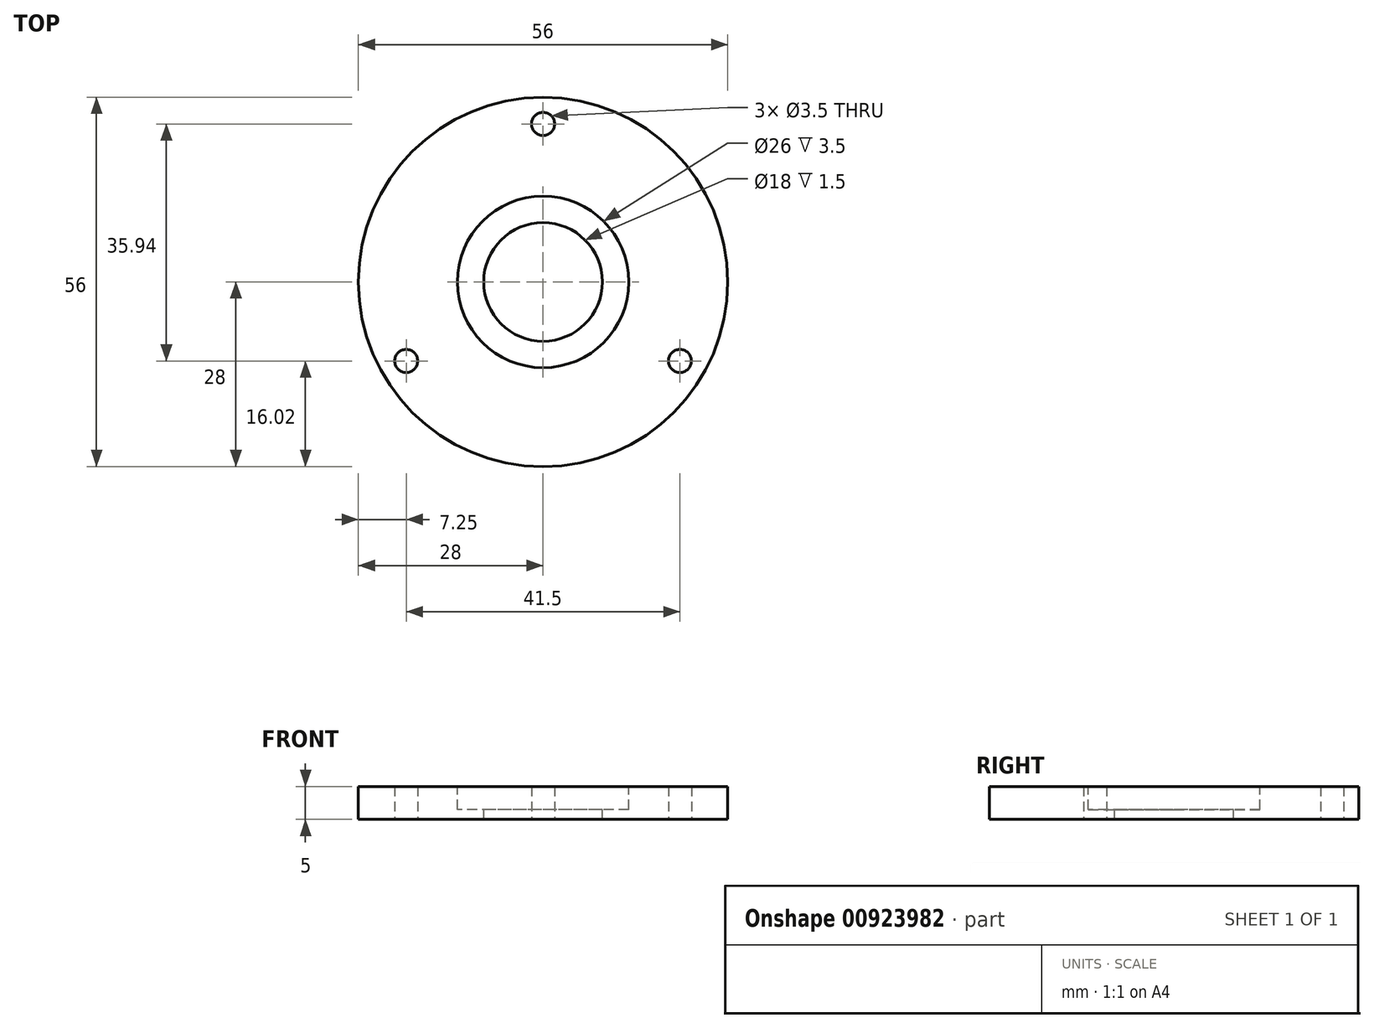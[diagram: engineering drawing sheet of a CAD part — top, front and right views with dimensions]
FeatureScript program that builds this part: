
annotation { "Feature Type Name" : "Feature", "Feature Type Description" : "" }
export const myFeature = defineFeature(function(context is Context, id is Id, definition is map)
    precondition{}
    {
        {
            var Q0;
            Q0=qCreatedBy(makeId("Top.planeOp"),FACE);
            var sketch = newSketch(context, id + "F0", { "sketchPlane" : qUnion([Q0])});
            skCircle(sketch, "E0.cCircle", {"center": v(0, 0) * mm, "radius": 23.96 * mm, "construction": true});
            skLineSegment(sketch, "E0.0", {"start": v(0, 23.96) * mm, "end": v(20.75, -11.98) * mm, "construction": true});
            skLineSegment(sketch, "E0.1", {"start": v(20.75, -11.98) * mm, "end": v(-20.75, -11.98) * mm, "construction": true});
            skLineSegment(sketch, "E0.2", {"start": v(-20.75, -11.98) * mm, "end": v(0, 23.96) * mm, "construction": true});
            skCircle(sketch, "E1", {"center": v(0, 23.96) * mm, "radius": 1.75 * mm});
            skCircle(sketch, "E2", {"center": v(-20.75, -11.98) * mm, "radius": 1.75 * mm});
            skCircle(sketch, "E3", {"center": v(20.75, -11.98) * mm, "radius": 1.75 * mm});
            skPoint(sketch, "E4.visualSharp", {"position": v(0, 33.78) * mm});
            skPoint(sketch, "E5.visualSharp", {"position": v(29.26, -16.9) * mm});
            skPoint(sketch, "E6.visualSharp", {"position": v(-29.26, -16.9) * mm});
            skCircle(sketch, "E7", {"center": v(0, 0) * mm, "radius": 28 * mm});
            skSolve(sketch);
        }
        {
            var Q0;
            Q0=makeQuery(id+"F0.imprint","IMPRINT",FACE,{"disambiguationData":[TD([[makeQuery(id+"F0.imprint","IMPRINT",EDGE,{"derivedFrom":sQuery(id+"F0.wireOp",EDGE,"ea9becb2-c0e6-4b76-8b01-0c3d61702e1b.0")}),-1.0]])]});
            var Q1;
            Q1=makeQuery(id+"F0.imprint","IMPRINT",FACE,{"disambiguationData":[TD([[makeQuery(id+"F0.imprint","IMPRINT",EDGE,{"derivedFrom":sQuery(id+"F0.wireOp",EDGE,"E1")}),-1.0]])]});
            extrude(context, id + "F1", {"entities" : qUnion([Q0, Q1]), "depth" : 5 * mm, "offsetDistance" : 25 * mm});
        }
        {
            var Q0;
            Q0=makeQuery(id+"F1.opExtrude","CAP_FACE",FACE,{"disambiguationData":[OSD([sQuery(id+"F0.wireOp",EDGE,"E1"),sQuery(id+"F0.wireOp",EDGE,"E2"),sQuery(id+"F0.wireOp",EDGE,"E3"),sQuery(id+"F0.wireOp",EDGE,"E7")])],"isStart":false});
            var sketch = newSketch(context, id + "F2", { "sketchPlane" : qUnion([Q0])});
            skCircle(sketch, "E8", {"center": v(0, 0) * mm, "radius": 13 * mm});
            skSolve(sketch);
        }
        {
            var Q0;
            Q0=makeQuery(id+"F2.imprint","IMPRINT",FACE,{"disambiguationData":[TD([[makeQuery(id+"F2.imprint","IMPRINT",EDGE,{"derivedFrom":sQuery(id+"F2.wireOp",EDGE,"E8")}),1.0]])]});
            extrude(context, id + "F3", {"entities" : qUnion([Q0]), "operationType" : NewBodyOperationType.REMOVE, "oppositeDirection" : true, "depth" : 3.5 * mm, "offsetDistance" : 25 * mm});
        }
        {
            var Q0;
            Q0=makeQuery(id+"F3.boolean.opBoolean","COPY",FACE,{"derivedFrom":makeQuery(id+"F3.opExtrude","CAP_FACE",FACE,{"disambiguationData":[OSD([sQuery(id+"F2.wireOp",EDGE,"E8")])],"isStart":false})});
            var sketch = newSketch(context, id + "F4", { "sketchPlane" : qUnion([Q0])});
            skCircle(sketch, "E9", {"center": v(0, 0) * mm, "radius": 9 * mm});
            skSolve(sketch);
        }
        {
            var Q0;
            Q0=makeQuery(id+"F4.imprint","IMPRINT",FACE,{"disambiguationData":[TD([[makeQuery(id+"F4.imprint","IMPRINT",EDGE,{"derivedFrom":sQuery(id+"F4.wireOp",EDGE,"E9")}),1.0]])]});
            extrude(context, id + "F5", {"entities" : qUnion([Q0]), "operationType" : NewBodyOperationType.REMOVE, "endBound" : BoundingType.THROUGH_ALL, "oppositeDirection" : true, "depth" : 25 * mm, "offsetDistance" : 25 * mm});
        }
    });
